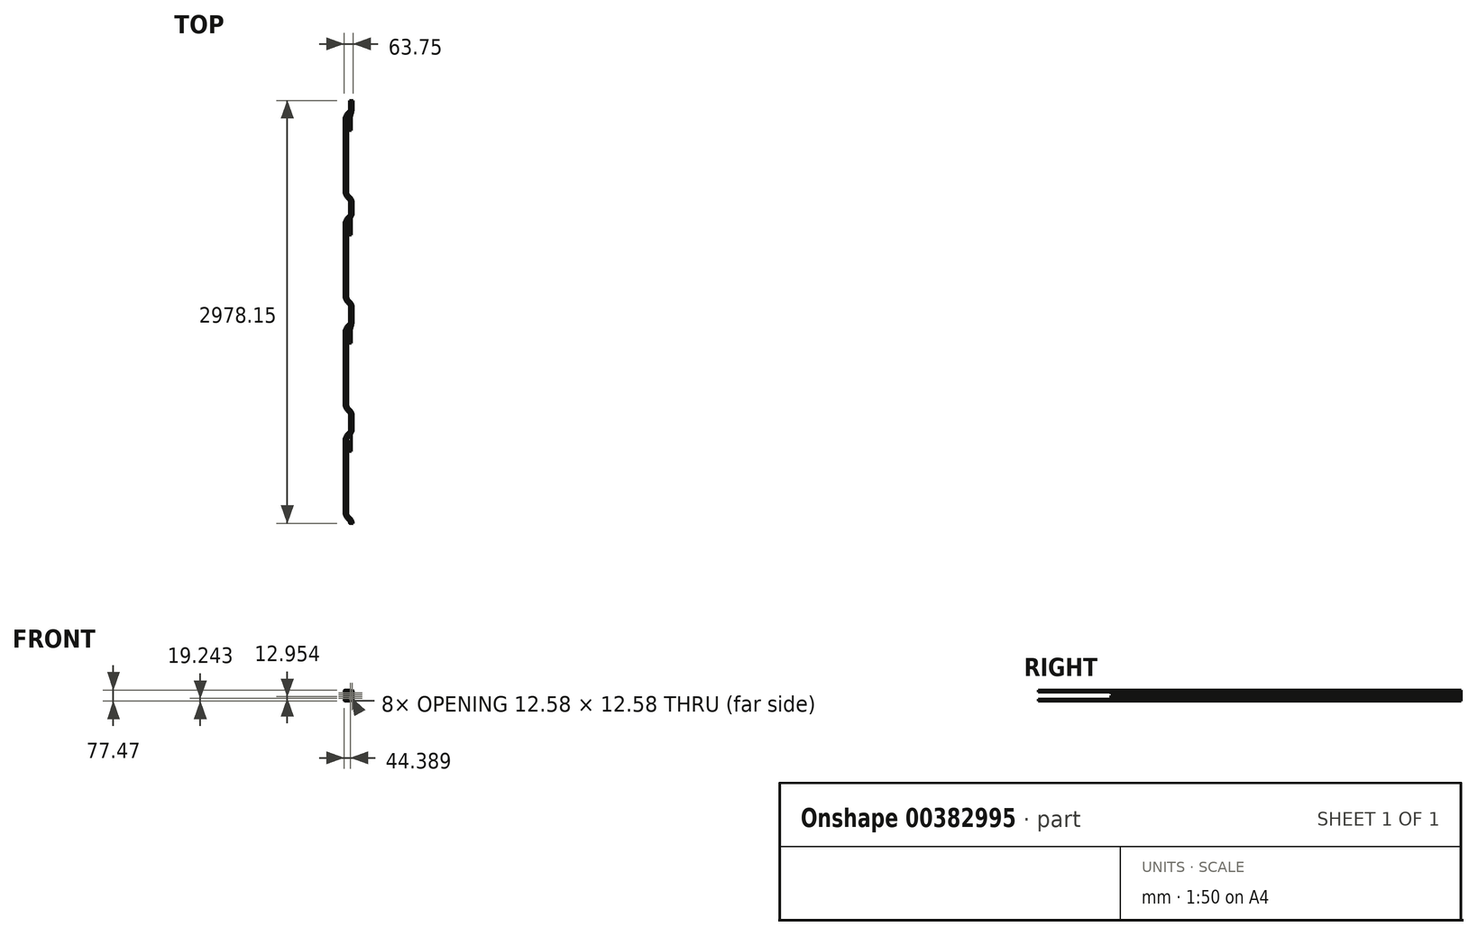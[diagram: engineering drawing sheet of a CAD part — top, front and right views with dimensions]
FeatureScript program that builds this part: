
annotation { "Feature Type Name" : "Feature", "Feature Type Description" : "" }
export const myFeature = defineFeature(function(context is Context, id is Id, definition is map)
    precondition{}
    {
        {
            var Q0;
            Q0=qCreatedBy(makeId("Front.planeOp"),FACE);
            var sketch = newSketch(context, id + "F0", { "sketchPlane" : qUnion([Q0])});
            skCircle(sketch, "E0", {"center": v(0, 0) * mm, "radius": 6.35 * mm});
            skCircle(sketch, "E1.0.1.0", {"center": v(0, -12.95) * mm, "radius": 6.35 * mm});
            skCircle(sketch, "E1.0.2.0", {"center": v(0, -25.9) * mm, "radius": 6.35 * mm});
            skCircle(sketch, "E1.0.3.0", {"center": v(0, -38.86) * mm, "radius": 6.35 * mm});
            skCircle(sketch, "E1.0.4.0", {"center": v(0, -51.82) * mm, "radius": 6.35 * mm});
            skCircle(sketch, "E1.0.5.0", {"center": v(0, -64.77) * mm, "radius": 6.35 * mm});
            skCircle(sketch, "E1.1.0.0", {"center": v(12.95, 0) * mm, "radius": 6.35 * mm});
            skCircle(sketch, "E1.1.1.0", {"center": v(12.95, -12.95) * mm, "radius": 6.35 * mm});
            skCircle(sketch, "E1.1.2.0", {"center": v(12.95, -25.9) * mm, "radius": 6.35 * mm});
            skCircle(sketch, "E1.1.3.0", {"center": v(12.95, -38.86) * mm, "radius": 6.35 * mm});
            skCircle(sketch, "E1.1.4.0", {"center": v(12.95, -51.82) * mm, "radius": 6.35 * mm});
            skCircle(sketch, "E1.1.5.0", {"center": v(12.95, -64.77) * mm, "radius": 6.35 * mm});
            skLineSegment(sketch, "E1.direction1", {"start": v(0, 0) * mm, "end": v(12.95, 0) * mm, "construction": true});
            skLineSegment(sketch, "E1.direction2", {"start": v(0, 0) * mm, "end": v(0, -12.95) * mm, "construction": true});
            skLineSegment(sketch, "E2", {"start": v(12.95, 6.35) * mm, "end": v(0, 6.35) * mm});
            skLineSegment(sketch, "E3", {"start": v(12.95, -71.12) * mm, "end": v(0, -71.12) * mm});
            skLineSegment(sketch, "E4", {"start": v(19.3, -64.77) * mm, "end": v(19.3, 0) * mm});
            skLineSegment(sketch, "E5", {"start": v(-6.35, -64.77) * mm, "end": v(-6.35, 0) * mm});
            skArc(sketch, "E6", {"start": v(-6.35, 0) * mm, "mid": v(-4.5, 4.5) * mm, "end": v(0, 6.35) * mm});
            skArc(sketch, "E7", {"start": v(19.3, 0) * mm, "mid": v(17.44, 4.5) * mm, "end": v(12.95, 6.35) * mm});
            skArc(sketch, "E8", {"start": v(0, -71.12) * mm, "mid": v(-4.5, -69.26) * mm, "end": v(-6.35, -64.77) * mm});
            skArc(sketch, "E9", {"start": v(12.95, -71.12) * mm, "mid": v(17.44, -69.26) * mm, "end": v(19.3, -64.77) * mm});
            skSolve(sketch);
        }
        {
            var Q0;
            {var subQ0=sQuery(id+"F0.wireOp",EDGE,"E1.1.0.0");var subQ1=makeQuery(id+"F0.imprint","INTERSECT",VERTEX,{"derivedFrom":[subQ0,sQuery(id+"F0.wireOp",EDGE,"E2")]});Q0=makeQuery(id+"F0.imprint","IMPRINT",FACE,{"disambiguationData":[TD([[makeQuery(id+"F0.imprint","IMPRINT",EDGE,{"disambiguationData":[TD([[subQ1,1.0]])],"derivedFrom":subQ0}),1.0]])]});}
            var Q1;
            {var subQ0=sQuery(id+"F0.wireOp",EDGE,"E0");var subQ1=makeQuery(id+"F0.imprint","INTERSECT",VERTEX,{"derivedFrom":[subQ0,sQuery(id+"F0.wireOp",EDGE,"E2")]});Q1=makeQuery(id+"F0.imprint","IMPRINT",FACE,{"disambiguationData":[TD([[makeQuery(id+"F0.imprint","IMPRINT",EDGE,{"disambiguationData":[TD([[subQ1,-1.0]])],"derivedFrom":subQ0}),1.0]])]});}
            var Q2;
            Q2=makeQuery(id+"F0.imprint","IMPRINT",FACE,{"disambiguationData":[TD([[makeQuery(id+"F0.imprint","IMPRINT",EDGE,{"derivedFrom":sQuery(id+"F0.wireOp",EDGE,"E1.1.1.0")}),1.0]])]});
            var Q3;
            Q3=makeQuery(id+"F0.imprint","IMPRINT",FACE,{"disambiguationData":[TD([[makeQuery(id+"F0.imprint","IMPRINT",EDGE,{"derivedFrom":sQuery(id+"F0.wireOp",EDGE,"E1.0.1.0")}),1.0]])]});
            var Q4;
            Q4=makeQuery(id+"F0.imprint","IMPRINT",FACE,{"disambiguationData":[TD([[makeQuery(id+"F0.imprint","IMPRINT",EDGE,{"derivedFrom":sQuery(id+"F0.wireOp",EDGE,"E1.1.2.0")}),1.0]])]});
            var Q5;
            Q5=makeQuery(id+"F0.imprint","IMPRINT",FACE,{"disambiguationData":[TD([[makeQuery(id+"F0.imprint","IMPRINT",EDGE,{"derivedFrom":sQuery(id+"F0.wireOp",EDGE,"E1.0.2.0")}),1.0]])]});
            var Q6;
            Q6=makeQuery(id+"F0.imprint","IMPRINT",FACE,{"disambiguationData":[TD([[makeQuery(id+"F0.imprint","IMPRINT",EDGE,{"derivedFrom":sQuery(id+"F0.wireOp",EDGE,"E1.1.3.0")}),1.0]])]});
            var Q7;
            Q7=makeQuery(id+"F0.imprint","IMPRINT",FACE,{"disambiguationData":[TD([[makeQuery(id+"F0.imprint","IMPRINT",EDGE,{"derivedFrom":sQuery(id+"F0.wireOp",EDGE,"E1.0.3.0")}),1.0]])]});
            var Q8;
            Q8=makeQuery(id+"F0.imprint","IMPRINT",FACE,{"disambiguationData":[TD([[makeQuery(id+"F0.imprint","IMPRINT",EDGE,{"derivedFrom":sQuery(id+"F0.wireOp",EDGE,"E1.1.4.0")}),1.0]])]});
            var Q9;
            Q9=makeQuery(id+"F0.imprint","IMPRINT",FACE,{"disambiguationData":[TD([[makeQuery(id+"F0.imprint","IMPRINT",EDGE,{"derivedFrom":sQuery(id+"F0.wireOp",EDGE,"E1.0.4.0")}),1.0]])]});
            var Q10;
            {var subQ0=sQuery(id+"F0.wireOp",EDGE,"E1.1.5.0");var subQ1=makeQuery(id+"F0.imprint","INTERSECT",VERTEX,{"derivedFrom":[subQ0,sQuery(id+"F0.wireOp",EDGE,"E3")]});Q10=makeQuery(id+"F0.imprint","IMPRINT",FACE,{"disambiguationData":[TD([[makeQuery(id+"F0.imprint","IMPRINT",EDGE,{"disambiguationData":[TD([[subQ1,1.0]])],"derivedFrom":subQ0}),1.0]])]});}
            var Q11;
            {var subQ0=sQuery(id+"F0.wireOp",EDGE,"E1.0.5.0");var subQ1=makeQuery(id+"F0.imprint","INTERSECT",VERTEX,{"derivedFrom":[subQ0,sQuery(id+"F0.wireOp",EDGE,"E3")]});Q11=makeQuery(id+"F0.imprint","IMPRINT",FACE,{"disambiguationData":[TD([[makeQuery(id+"F0.imprint","IMPRINT",EDGE,{"disambiguationData":[TD([[subQ1,1.0]])],"derivedFrom":subQ0}),1.0]])]});}
            extrude(context, id + "F1", {"entities" : qUnion([Q0, Q1, Q2, Q3, Q4, Q5, Q6, Q7, Q8, Q9, Q10, Q11]), "oppositeDirection" : true, "depth" : 6.35 * mm});
        }
        {
            var Q0;
            {var subQ24=sQuery(id+"F0.wireOp",EDGE,"E1.0.1.0");Q0=makeQuery(id+"F0.imprint","IMPRINT",FACE,{"disambiguationData":[TD([[makeQuery(id+"F0.imprint","IMPRINT",EDGE,{"derivedFrom":subQ24}),-1.0]])]});}
            var Q1;
            Q1=makeQuery(id+"F0.imprint","IMPRINT",FACE,{"disambiguationData":[TD([[makeQuery(id+"F0.imprint","IMPRINT",EDGE,{"derivedFrom":sQuery(id+"F0.wireOp",EDGE,"E1.1.4.0")}),1.0]])]});
            var Q2;
            Q2=makeQuery(id+"F0.imprint","IMPRINT",FACE,{"disambiguationData":[TD([[makeQuery(id+"F0.imprint","IMPRINT",EDGE,{"derivedFrom":sQuery(id+"F0.wireOp",EDGE,"E1.0.4.0")}),1.0]])]});
            var Q3;
            {var subQ0=sQuery(id+"F0.wireOp",EDGE,"E1.1.5.0");var subQ1=makeQuery(id+"F0.imprint","INTERSECT",VERTEX,{"derivedFrom":[subQ0,sQuery(id+"F0.wireOp",EDGE,"E3")]});Q3=makeQuery(id+"F0.imprint","IMPRINT",FACE,{"disambiguationData":[TD([[makeQuery(id+"F0.imprint","IMPRINT",EDGE,{"disambiguationData":[TD([[subQ1,1.0]])],"derivedFrom":subQ0}),1.0]])]});}
            var Q4;
            {var subQ0=sQuery(id+"F0.wireOp",EDGE,"E1.0.5.0");var subQ1=makeQuery(id+"F0.imprint","INTERSECT",VERTEX,{"derivedFrom":[subQ0,sQuery(id+"F0.wireOp",EDGE,"E3")]});Q4=makeQuery(id+"F0.imprint","IMPRINT",FACE,{"disambiguationData":[TD([[makeQuery(id+"F0.imprint","IMPRINT",EDGE,{"disambiguationData":[TD([[subQ1,1.0]])],"derivedFrom":subQ0}),1.0]])]});}
            var Q5;
            Q5=makeQuery(id+"F0.imprint","IMPRINT",FACE,{"disambiguationData":[TD([[makeQuery(id+"F0.imprint","IMPRINT",EDGE,{"derivedFrom":sQuery(id+"F0.wireOp",EDGE,"E1.0.3.0")}),1.0]])]});
            var Q6;
            Q6=makeQuery(id+"F0.imprint","IMPRINT",FACE,{"disambiguationData":[TD([[makeQuery(id+"F0.imprint","IMPRINT",EDGE,{"derivedFrom":sQuery(id+"F0.wireOp",EDGE,"E1.1.3.0")}),1.0]])]});
            var Q7;
            Q7=makeQuery(id+"F0.imprint","IMPRINT",FACE,{"disambiguationData":[TD([[makeQuery(id+"F0.imprint","IMPRINT",EDGE,{"derivedFrom":sQuery(id+"F0.wireOp",EDGE,"E1.1.2.0")}),1.0]])]});
            var Q8;
            Q8=makeQuery(id+"F0.imprint","IMPRINT",FACE,{"disambiguationData":[TD([[makeQuery(id+"F0.imprint","IMPRINT",EDGE,{"derivedFrom":sQuery(id+"F0.wireOp",EDGE,"E1.0.2.0")}),1.0]])]});
            var Q9;
            Q9=makeQuery(id+"F0.imprint","IMPRINT",FACE,{"disambiguationData":[TD([[makeQuery(id+"F0.imprint","IMPRINT",EDGE,{"derivedFrom":sQuery(id+"F0.wireOp",EDGE,"E1.1.1.0")}),1.0]])]});
            var Q10;
            Q10=makeQuery(id+"F0.imprint","IMPRINT",FACE,{"disambiguationData":[TD([[makeQuery(id+"F0.imprint","IMPRINT",EDGE,{"derivedFrom":sQuery(id+"F0.wireOp",EDGE,"E1.0.1.0")}),1.0]])]});
            var Q11;
            {var subQ0=sQuery(id+"F0.wireOp",EDGE,"E0");var subQ1=makeQuery(id+"F0.imprint","INTERSECT",VERTEX,{"derivedFrom":[subQ0,sQuery(id+"F0.wireOp",EDGE,"E2")]});Q11=makeQuery(id+"F0.imprint","IMPRINT",FACE,{"disambiguationData":[TD([[makeQuery(id+"F0.imprint","IMPRINT",EDGE,{"disambiguationData":[TD([[subQ1,-1.0]])],"derivedFrom":subQ0}),1.0]])]});}
            var Q12;
            {var subQ0=sQuery(id+"F0.wireOp",EDGE,"E1.1.0.0");var subQ1=makeQuery(id+"F0.imprint","INTERSECT",VERTEX,{"derivedFrom":[subQ0,sQuery(id+"F0.wireOp",EDGE,"E2")]});Q12=makeQuery(id+"F0.imprint","IMPRINT",FACE,{"disambiguationData":[TD([[makeQuery(id+"F0.imprint","IMPRINT",EDGE,{"disambiguationData":[TD([[subQ1,1.0]])],"derivedFrom":subQ0}),1.0]])]});}
            extrude(context, id + "F2", {"entities" : qUnion([Q0, Q1, Q2, Q3, Q4, Q5, Q6, Q7, Q8, Q9, Q10, Q11, Q12]), "operationType" : NewBodyOperationType.ADD, "oppositeDirection" : true, "depth" : 3.17 * mm});
        }
        {
            var Q0;
            Q0=qCreatedBy(makeId("Top.planeOp"),FACE);
            var sketch = newSketch(context, id + "F3", { "sketchPlane" : qUnion([Q0])});
            skPoint(sketch, "E10.0", {"position": v(12.95, 0) * mm});
            skPoint(sketch, "E11.0", {"position": v(0, 0) * mm});
            skPoint(sketch, "E12.0", {"position": v(6.48, 0) * mm});
            skLineSegment(sketch, "E13", {"start": v(12.95, 0) * mm, "end": v(12.95, -152.4) * mm});
            skPoint(sketch, "E14", {"position": v(-25.15, -76.2) * mm});
            skFitSpline(sketch, "E15", {"points": [v(-25.15, -76.2) * mm, v(12.95, 0) * mm], "startDerivative": vector(0, 114.3) * mm, "endDerivative": vector(0, 114.3) * mm});
            skPoint(sketch, "E16", {"position": v(-6.1, -38.1) * mm});
            skLineSegment(sketch, "E17", {"start": v(-25.15, -76.2) * mm, "end": v(-25.15, -584.2) * mm});
            skPoint(sketch, "E18", {"position": v(12.95, -660.4) * mm});
            skFitSpline(sketch, "E19", {"points": [v(-25.15, -584.2) * mm, v(12.95, -660.4) * mm], "startDerivative": vector(0, -114.3) * mm, "endDerivative": vector(0, -114.3) * mm});
            skPoint(sketch, "E20", {"position": v(-6.1, -622.3) * mm});
            skLineSegment(sketch, "E21", {"start": v(12.95, -660.4) * mm, "end": v(12.95, -889) * mm});
            skFitSpline(sketch, "E22", {"points": [v(12.95, 0) * mm, v(0, -76.2) * mm], "startDerivative": vector(0, -114.3) * mm, "endDerivative": vector(0, -114.3) * mm});
            skLineSegment(sketch, "E23", {"start": v(0, -76.2) * mm, "end": v(0, -152.4) * mm});
            skLineSegment(sketch, "E24", {"start": v(12.95, -660.4) * mm, "end": v(12.95, -736.6) * mm});
            skPoint(sketch, "E25", {"position": v(-25.15, -812.8) * mm});
            skFitSpline(sketch, "E26", {"points": [v(-25.15, -812.8) * mm, v(12.95, -736.6) * mm], "startDerivative": vector(0, 114.3) * mm, "endDerivative": vector(0, 114.3) * mm});
            skPoint(sketch, "E27", {"position": v(-6.1, -774.7) * mm});
            skLineSegment(sketch, "E28", {"start": v(-25.15, -812.8) * mm, "end": v(-25.15, -1320.8) * mm});
            skPoint(sketch, "E29", {"position": v(12.95, -1397) * mm});
            skPoint(sketch, "E30", {"position": v(-6.1, -1358.9) * mm});
            skLineSegment(sketch, "E31", {"start": v(12.95, -1397) * mm, "end": v(12.95, -1498.6) * mm});
            skPoint(sketch, "E32", {"position": v(-6.1, -1536.7) * mm});
            skPoint(sketch, "E33", {"position": v(-25.15, -1574.8) * mm});
            skPoint(sketch, "E34", {"position": v(12.95, -1498.6) * mm});
            skPoint(sketch, "E35", {"position": v(-25.15, -1320.8) * mm});
            skFitSpline(sketch, "E36", {"points": [v(-25.15, -1320.8) * mm, v(12.95, -1397) * mm], "startDerivative": vector(0, -114.3) * mm, "endDerivative": vector(0, -114.3) * mm});
            skFitSpline(sketch, "E37", {"points": [v(12.95, -1498.6) * mm, v(-25.15, -1574.8) * mm], "startDerivative": vector(0, -114.3) * mm, "endDerivative": vector(0, -114.3) * mm});
            skPoint(sketch, "E38", {"position": v(0, -1574.8) * mm});
            skFitSpline(sketch, "E39", {"points": [v(12.95, -1498.6) * mm, v(0, -1574.8) * mm], "startDerivative": vector(0, -114.3) * mm, "endDerivative": vector(0, -114.3) * mm});
            skLineSegment(sketch, "E40", {"start": v(0, -1574.8) * mm, "end": v(0, -1651) * mm});
            skLineSegment(sketch, "E41", {"start": v(-25.15, -1574.8) * mm, "end": v(-25.15, -2082.8) * mm});
            skPoint(sketch, "E42", {"position": v(12.95, -2159) * mm});
            skPoint(sketch, "E43", {"position": v(12.95, -2260.6) * mm});
            skPoint(sketch, "E44", {"position": v(-25.15, -2336.8) * mm});
            skPoint(sketch, "E45", {"position": v(-25.15, -2844.8) * mm});
            skPoint(sketch, "E46", {"position": v(12.95, -2921) * mm});
            skPoint(sketch, "E47", {"position": v(-25.15, -2120.9) * mm});
            skPoint(sketch, "E48", {"position": v(-25.15, -2298.7) * mm});
            skFitSpline(sketch, "E49", {"points": [v(-25.15, -2082.8) * mm, v(12.95, -2159) * mm], "startDerivative": vector(0, -114.3) * mm, "endDerivative": vector(0, -114.3) * mm});
            skFitSpline(sketch, "E50", {"points": [v(12.95, -2260.6) * mm, v(-25.15, -2336.8) * mm], "startDerivative": vector(0, -114.3) * mm, "endDerivative": vector(0, -114.3) * mm});
            skLineSegment(sketch, "E51", {"start": v(12.95, -2159) * mm, "end": v(12.95, -2260.6) * mm});
            skPoint(sketch, "E52", {"position": v(-25.15, -2882.9) * mm});
            skLineSegment(sketch, "E53", {"start": v(12.95, -2260.6) * mm, "end": v(12.95, -2336.8) * mm});
            skLineSegment(sketch, "E54", {"start": v(12.95, -2336.8) * mm, "end": v(12.95, -2413) * mm});
            skFitSpline(sketch, "E55", {"points": [v(-25.15, -2844.8) * mm, v(12.95, -2921) * mm], "startDerivative": vector(0, -114.3) * mm, "endDerivative": vector(0, -114.3) * mm});
            skLineSegment(sketch, "E56", {"start": v(-25.15, -2336.8) * mm, "end": v(-25.15, -2844.8) * mm});
            skSolve(sketch);
        }
        {
            var Q0;
            Q0=makeQuery(id+"F0.imprint","IMPRINT",FACE,{"disambiguationData":[TD([[makeQuery(id+"F0.imprint","IMPRINT",EDGE,{"derivedFrom":sQuery(id+"F0.wireOp",EDGE,"E1.1.1.0")}),1.0]])]});
            var Q1;
            Q1=makeQuery(id+"F0.imprint","IMPRINT",FACE,{"disambiguationData":[TD([[makeQuery(id+"F0.imprint","IMPRINT",EDGE,{"derivedFrom":sQuery(id+"F0.wireOp",EDGE,"E1.1.3.0")}),1.0]])]});
            var Q2;
            Q2=sQuery(id+"F3.wireOp",EDGE,"E22");
            var Q3;
            Q3=sQuery(id+"F3.wireOp",EDGE,"E23");
            sweep(context, id + "F4", {"operationType" : NewBodyOperationType.ADD, "profiles" : qUnion([Q0, Q1]), "path" : qUnion([Q2, Q3])});
        }
        {
            var Q0;
            {var subQ0=sQuery(id+"F0.wireOp",EDGE,"E0");var subQ1=makeQuery(id+"F0.imprint","INTERSECT",VERTEX,{"derivedFrom":[subQ0,sQuery(id+"F0.wireOp",EDGE,"E2")]});Q0=makeQuery(id+"F0.imprint","IMPRINT",FACE,{"disambiguationData":[TD([[makeQuery(id+"F0.imprint","IMPRINT",EDGE,{"disambiguationData":[TD([[subQ1,-1.0]])],"derivedFrom":subQ0}),1.0]])]});}
            var Q1;
            {var subQ0=sQuery(id+"F0.wireOp",EDGE,"E1.1.0.0");var subQ1=makeQuery(id+"F0.imprint","INTERSECT",VERTEX,{"derivedFrom":[subQ0,sQuery(id+"F0.wireOp",EDGE,"E2")]});Q1=makeQuery(id+"F0.imprint","IMPRINT",FACE,{"disambiguationData":[TD([[makeQuery(id+"F0.imprint","IMPRINT",EDGE,{"disambiguationData":[TD([[subQ1,1.0]])],"derivedFrom":subQ0}),1.0]])]});}
            var Q2;
            Q2=makeQuery(id+"F0.imprint","IMPRINT",FACE,{"disambiguationData":[TD([[makeQuery(id+"F0.imprint","IMPRINT",EDGE,{"derivedFrom":sQuery(id+"F0.wireOp",EDGE,"E1.0.1.0")}),1.0]])]});
            var Q3;
            Q3=makeQuery(id+"F0.imprint","IMPRINT",FACE,{"disambiguationData":[TD([[makeQuery(id+"F0.imprint","IMPRINT",EDGE,{"derivedFrom":sQuery(id+"F0.wireOp",EDGE,"E1.1.2.0")}),1.0]])]});
            var Q4;
            Q4=makeQuery(id+"F0.imprint","IMPRINT",FACE,{"disambiguationData":[TD([[makeQuery(id+"F0.imprint","IMPRINT",EDGE,{"derivedFrom":sQuery(id+"F0.wireOp",EDGE,"E1.0.2.0")}),1.0]])]});
            var Q5;
            Q5=makeQuery(id+"F0.imprint","IMPRINT",FACE,{"disambiguationData":[TD([[makeQuery(id+"F0.imprint","IMPRINT",EDGE,{"derivedFrom":sQuery(id+"F0.wireOp",EDGE,"E1.0.3.0")}),1.0]])]});
            var Q6;
            Q6=makeQuery(id+"F0.imprint","IMPRINT",FACE,{"disambiguationData":[TD([[makeQuery(id+"F0.imprint","IMPRINT",EDGE,{"derivedFrom":sQuery(id+"F0.wireOp",EDGE,"E1.0.4.0")}),1.0]])]});
            var Q7;
            {var subQ0=sQuery(id+"F0.wireOp",EDGE,"E1.0.5.0");var subQ1=makeQuery(id+"F0.imprint","INTERSECT",VERTEX,{"derivedFrom":[subQ0,sQuery(id+"F0.wireOp",EDGE,"E3")]});Q7=makeQuery(id+"F0.imprint","IMPRINT",FACE,{"disambiguationData":[TD([[makeQuery(id+"F0.imprint","IMPRINT",EDGE,{"disambiguationData":[TD([[subQ1,1.0]])],"derivedFrom":subQ0}),1.0]])]});}
            var Q8;
            Q8=makeQuery(id+"F0.imprint","IMPRINT",FACE,{"disambiguationData":[TD([[makeQuery(id+"F0.imprint","IMPRINT",EDGE,{"derivedFrom":sQuery(id+"F0.wireOp",EDGE,"E1.1.4.0")}),1.0]])]});
            var Q9;
            {var subQ0=sQuery(id+"F0.wireOp",EDGE,"E1.1.5.0");var subQ1=makeQuery(id+"F0.imprint","INTERSECT",VERTEX,{"derivedFrom":[subQ0,sQuery(id+"F0.wireOp",EDGE,"E3")]});Q9=makeQuery(id+"F0.imprint","IMPRINT",FACE,{"disambiguationData":[TD([[makeQuery(id+"F0.imprint","IMPRINT",EDGE,{"disambiguationData":[TD([[subQ1,1.0]])],"derivedFrom":subQ0}),1.0]])]});}
            var Q10;
            Q10=sQuery(id+"F3.wireOp",EDGE,"E15");
            var Q11;
            Q11=sQuery(id+"F3.wireOp",EDGE,"E17");
            var Q12;
            Q12=sQuery(id+"F3.wireOp",EDGE,"E19");
            sweep(context, id + "F5", {"operationType" : NewBodyOperationType.ADD, "profiles" : qUnion([Q0, Q1, Q2, Q3, Q4, Q5, Q6, Q7, Q8, Q9]), "path" : qUnion([Q10, Q11, Q12])});
        }
        {
            var Q0;
            Q0=makeQuery(id+"F5.opSweep","CAP_FACE",FACE,{"disambiguationData":[OSD([sQuery(id+"F0.wireOp",EDGE,"E1.0.1.0"),sQuery(id+"F3.wireOp",VERTEX,"E19.end")])],"isStart":false});
            var Q1;
            Q1=makeQuery(id+"F5.opSweep","CAP_FACE",FACE,{"disambiguationData":[OSD([sQuery(id+"F0.wireOp",EDGE,"E1.0.3.0"),sQuery(id+"F3.wireOp",VERTEX,"E19.end")])],"isStart":false});
            var Q2;
            Q2=sQuery(id+"F3.wireOp",EDGE,"E21");
            sweep(context, id + "F6", {"operationType" : NewBodyOperationType.ADD, "profiles" : qUnion([Q0, Q1]), "path" : qUnion([Q2])});
        }
        {
            var Q0;
            Q0=makeQuery(id+"F5.opSweep","CAP_FACE",FACE,{"disambiguationData":[OSD([sQuery(id+"F0.wireOp",EDGE,"E1.1.0.0"),sQuery(id+"F3.wireOp",VERTEX,"E19.end")])],"isStart":false});
            var Q1;
            Q1=makeQuery(id+"F5.opSweep","CAP_FACE",FACE,{"disambiguationData":[OSD([sQuery(id+"F0.wireOp",EDGE,"E0"),sQuery(id+"F3.wireOp",VERTEX,"E19.end")])],"isStart":false});
            var Q2;
            Q2=makeQuery(id+"F5.opSweep","CAP_FACE",FACE,{"disambiguationData":[OSD([sQuery(id+"F0.wireOp",EDGE,"E1.0.2.0"),sQuery(id+"F3.wireOp",VERTEX,"E19.end")])],"isStart":false});
            var Q3;
            Q3=makeQuery(id+"F5.opSweep","CAP_FACE",FACE,{"disambiguationData":[OSD([sQuery(id+"F0.wireOp",EDGE,"E1.1.2.0"),sQuery(id+"F3.wireOp",VERTEX,"E19.end")])],"isStart":false});
            var Q4;
            Q4=makeQuery(id+"F5.opSweep","CAP_FACE",FACE,{"disambiguationData":[OSD([sQuery(id+"F0.wireOp",EDGE,"E1.0.4.0"),sQuery(id+"F3.wireOp",VERTEX,"E19.end")])],"isStart":false});
            var Q5;
            Q5=makeQuery(id+"F5.opSweep","CAP_FACE",FACE,{"disambiguationData":[OSD([sQuery(id+"F0.wireOp",EDGE,"E1.1.4.0"),sQuery(id+"F3.wireOp",VERTEX,"E19.end")])],"isStart":false});
            var Q6;
            Q6=makeQuery(id+"F5.opSweep","CAP_FACE",FACE,{"disambiguationData":[OSD([sQuery(id+"F0.wireOp",EDGE,"E1.0.5.0"),sQuery(id+"F3.wireOp",VERTEX,"E19.end")])],"isStart":false});
            var Q7;
            Q7=makeQuery(id+"F5.opSweep","CAP_FACE",FACE,{"disambiguationData":[OSD([sQuery(id+"F0.wireOp",EDGE,"E1.1.5.0"),sQuery(id+"F3.wireOp",VERTEX,"E19.end")])],"isStart":false});
            var Q8;
            Q8=sQuery(id+"F3.wireOp",EDGE,"E24");
            var Q9;
            Q9=sQuery(id+"F3.wireOp",EDGE,"E26");
            var Q10;
            Q10=sQuery(id+"F3.wireOp",EDGE,"E28");
            var Q11;
            Q11=sQuery(id+"F3.wireOp",EDGE,"E36");
            var Q12;
            Q12=sQuery(id+"F3.wireOp",EDGE,"E31");
            sweep(context, id + "F7", {"operationType" : NewBodyOperationType.ADD, "profiles" : qUnion([Q0, Q1, Q2, Q3, Q4, Q5, Q6, Q7]), "path" : qUnion([Q8, Q9, Q10, Q11, Q12])});
        }
        {
            var Q0;
            Q0=qCreatedBy(makeId("Right.planeOp"),FACE);
            var sketch = newSketch(context, id + "F8", { "sketchPlane" : qUnion([Q0])});
            skFitSpline(sketch, "E57.0", {"points": [v(-1498.6, 0) * mm, v(-1536.7, 0) * mm, v(-1536.7, 0) * mm, v(-1574.8, 0) * mm]});
            skLineSegment(sketch, "E58.0", {"start": v(-1574.8, 0) * mm, "end": v(-1651, 0) * mm});
            skPoint(sketch, "E59", {"position": v(-1651, 12.95) * mm});
            skPoint(sketch, "E60", {"position": v(-1612.9, 6.36) * mm});
            skPoint(sketch, "E60.positionSnap0", {"position": v(-1612.9, 0) * mm});
            skFitSpline(sketch, "E61", {"points": [v(-1574.8, 0) * mm, v(-1651, 12.95) * mm], "startDerivative": vector(-114.3, 0) * mm, "endDerivative": vector(-114.3, 0) * mm});
            skLineSegment(sketch, "E62.0", {"start": v(-2336.8, 0) * mm, "end": v(-2413, 0) * mm});
            skLineSegment(sketch, "E63.0", {"start": v(-2260.6, 0) * mm, "end": v(-2336.8, 0) * mm});
            skPoint(sketch, "E64", {"position": v(-2413, 12.95) * mm});
            skFitSpline(sketch, "E65", {"points": [v(-2336.8, 0) * mm, v(-2413, 12.95) * mm], "startDerivative": vector(-114.3, 0) * mm, "endDerivative": vector(-114.3, 0) * mm});
            skSolve(sketch);
        }
        {
            var Q0;
            Q0=makeQuery(id+"F7.opSweep","CAP_FACE",FACE,{"disambiguationData":[OSD([sQuery(id+"F0.wireOp",EDGE,"E1.1.0.0"),sQuery(id+"F3.wireOp",VERTEX,"E19.end"),sQuery(id+"F3.wireOp",VERTEX,"E31.end")])],"isStart":false});
            var Q1;
            Q1=makeQuery(id+"F7.opSweep","CAP_FACE",FACE,{"disambiguationData":[OSD([sQuery(id+"F0.wireOp",EDGE,"E0"),sQuery(id+"F3.wireOp",VERTEX,"E19.end"),sQuery(id+"F3.wireOp",VERTEX,"E31.end")])],"isStart":false});
            var Q2;
            Q2=makeQuery(id+"F7.opSweep","CAP_FACE",FACE,{"disambiguationData":[OSD([sQuery(id+"F0.wireOp",EDGE,"E1.0.5.0"),sQuery(id+"F3.wireOp",VERTEX,"E19.end"),sQuery(id+"F3.wireOp",VERTEX,"E31.end")])],"isStart":false});
            var Q3;
            Q3=makeQuery(id+"F7.opSweep","CAP_FACE",FACE,{"disambiguationData":[OSD([sQuery(id+"F0.wireOp",EDGE,"E1.1.5.0"),sQuery(id+"F3.wireOp",VERTEX,"E19.end"),sQuery(id+"F3.wireOp",VERTEX,"E31.end")])],"isStart":false});
            var Q4;
            Q4=makeQuery(id+"F7.opSweep","CAP_FACE",FACE,{"disambiguationData":[OSD([sQuery(id+"F0.wireOp",EDGE,"E1.0.4.0"),sQuery(id+"F3.wireOp",VERTEX,"E19.end"),sQuery(id+"F3.wireOp",VERTEX,"E31.end")])],"isStart":false});
            var Q5;
            Q5=makeQuery(id+"F7.opSweep","CAP_FACE",FACE,{"disambiguationData":[OSD([sQuery(id+"F0.wireOp",EDGE,"E1.0.2.0"),sQuery(id+"F3.wireOp",VERTEX,"E19.end"),sQuery(id+"F3.wireOp",VERTEX,"E31.end")])],"isStart":false});
            var Q6;
            Q6=sQuery(id+"F3.wireOp",EDGE,"E37");
            var Q7;
            Q7=sQuery(id+"F3.wireOp",EDGE,"E41");
            var Q8;
            Q8=sQuery(id+"F3.wireOp",EDGE,"E49");
            var Q9;
            Q9=sQuery(id+"F3.wireOp",EDGE,"E51");
            sweep(context, id + "F9", {"operationType" : NewBodyOperationType.ADD, "profiles" : qUnion([Q0, Q1, Q2, Q3, Q4, Q5]), "path" : qUnion([Q6, Q7, Q8, Q9])});
        }
        {
            var Q0;
            Q0=makeQuery(id+"F7.opSweep","CAP_FACE",FACE,{"disambiguationData":[OSD([sQuery(id+"F0.wireOp",EDGE,"E1.1.2.0"),sQuery(id+"F3.wireOp",VERTEX,"E19.end"),sQuery(id+"F3.wireOp",VERTEX,"E31.end")])],"isStart":false});
            var Q1;
            Q1=makeQuery(id+"F7.opSweep","CAP_FACE",FACE,{"disambiguationData":[OSD([sQuery(id+"F0.wireOp",EDGE,"E1.1.4.0"),sQuery(id+"F3.wireOp",VERTEX,"E19.end"),sQuery(id+"F3.wireOp",VERTEX,"E31.end")])],"isStart":false});
            var Q2;
            Q2=sQuery(id+"F3.wireOp",EDGE,"E39");
            var Q3;
            Q3=sQuery(id+"F8.wireOp",EDGE,"E61");
            sweep(context, id + "F10", {"operationType" : NewBodyOperationType.ADD, "profiles" : qUnion([Q0, Q1]), "path" : qUnion([Q2, Q3])});
        }
        {
            var Q0;
            Q0=makeQuery(id+"F9.opSweep","CAP_FACE",FACE,{"disambiguationData":[OSD([sQuery(id+"F0.wireOp",EDGE,"E1.1.0.0"),sQuery(id+"F3.wireOp",VERTEX,"E19.end"),sQuery(id+"F3.wireOp",VERTEX,"E31.end"),sQuery(id+"F3.wireOp",VERTEX,"E51.end")])],"isStart":false});
            var Q1;
            Q1=makeQuery(id+"F9.opSweep","CAP_FACE",FACE,{"disambiguationData":[OSD([sQuery(id+"F0.wireOp",EDGE,"E0"),sQuery(id+"F3.wireOp",VERTEX,"E19.end"),sQuery(id+"F3.wireOp",VERTEX,"E31.end"),sQuery(id+"F3.wireOp",VERTEX,"E51.end")])],"isStart":false});
            var Q2;
            Q2=makeQuery(id+"F9.opSweep","CAP_FACE",FACE,{"disambiguationData":[OSD([sQuery(id+"F0.wireOp",EDGE,"E1.1.5.0"),sQuery(id+"F3.wireOp",VERTEX,"E19.end"),sQuery(id+"F3.wireOp",VERTEX,"E31.end"),sQuery(id+"F3.wireOp",VERTEX,"E51.end")])],"isStart":false});
            var Q3;
            Q3=makeQuery(id+"F9.opSweep","CAP_FACE",FACE,{"disambiguationData":[OSD([sQuery(id+"F0.wireOp",EDGE,"E1.0.5.0"),sQuery(id+"F3.wireOp",VERTEX,"E19.end"),sQuery(id+"F3.wireOp",VERTEX,"E31.end"),sQuery(id+"F3.wireOp",VERTEX,"E51.end")])],"isStart":false});
            var Q4;
            Q4=sQuery(id+"F3.wireOp",EDGE,"E50");
            var Q5;
            Q5=sQuery(id+"F3.wireOp",EDGE,"E56");
            var Q6;
            Q6=sQuery(id+"F3.wireOp",EDGE,"E55");
            sweep(context, id + "F11", {"operationType" : NewBodyOperationType.ADD, "profiles" : qUnion([Q0, Q1, Q2, Q3]), "path" : qUnion([Q4, Q5, Q6])});
        }
        {
            var Q0;
            Q0=makeQuery(id+"F9.opSweep","CAP_FACE",FACE,{"disambiguationData":[OSD([sQuery(id+"F0.wireOp",EDGE,"E1.0.2.0"),sQuery(id+"F3.wireOp",VERTEX,"E19.end"),sQuery(id+"F3.wireOp",VERTEX,"E31.end"),sQuery(id+"F3.wireOp",VERTEX,"E51.end")])],"isStart":false});
            var Q1;
            Q1=makeQuery(id+"F9.opSweep","CAP_FACE",FACE,{"disambiguationData":[OSD([sQuery(id+"F0.wireOp",EDGE,"E1.0.4.0"),sQuery(id+"F3.wireOp",VERTEX,"E19.end"),sQuery(id+"F3.wireOp",VERTEX,"E31.end"),sQuery(id+"F3.wireOp",VERTEX,"E51.end")])],"isStart":false});
            var Q2;
            Q2=sQuery(id+"F8.wireOp",EDGE,"E63.0");
            var Q3;
            Q3=sQuery(id+"F8.wireOp",EDGE,"E65");
            sweep(context, id + "F12", {"operationType" : NewBodyOperationType.ADD, "profiles" : qUnion([Q0, Q1]), "path" : qUnion([Q2, Q3])});
        }
        {
            var Q0;
            Q0=makeQuery(id+"F1.opExtrude","CAP_FACE",FACE,{"disambiguationData":[OSD([sQuery(id+"F0.wireOp",EDGE,"E1.1.0.0")])],"isStart":false});
            var Q1;
            Q1=makeQuery(id+"F1.opExtrude","CAP_FACE",FACE,{"disambiguationData":[OSD([sQuery(id+"F0.wireOp",EDGE,"E0")])],"isStart":false});
            var Q2;
            Q2=makeQuery(id+"F1.opExtrude","CAP_FACE",FACE,{"disambiguationData":[OSD([sQuery(id+"F0.wireOp",EDGE,"E1.1.1.0")])],"isStart":false});
            var Q3;
            Q3=makeQuery(id+"F1.opExtrude","CAP_FACE",FACE,{"disambiguationData":[OSD([sQuery(id+"F0.wireOp",EDGE,"E1.0.1.0")])],"isStart":false});
            var Q4;
            Q4=makeQuery(id+"F1.opExtrude","CAP_FACE",FACE,{"disambiguationData":[OSD([sQuery(id+"F0.wireOp",EDGE,"E1.0.2.0")])],"isStart":false});
            var Q5;
            Q5=makeQuery(id+"F1.opExtrude","CAP_FACE",FACE,{"disambiguationData":[OSD([sQuery(id+"F0.wireOp",EDGE,"E1.1.2.0")])],"isStart":false});
            var Q6;
            Q6=makeQuery(id+"F1.opExtrude","CAP_FACE",FACE,{"disambiguationData":[OSD([sQuery(id+"F0.wireOp",EDGE,"E1.1.3.0")])],"isStart":false});
            var Q7;
            Q7=makeQuery(id+"F1.opExtrude","CAP_FACE",FACE,{"disambiguationData":[OSD([sQuery(id+"F0.wireOp",EDGE,"E1.0.3.0")])],"isStart":false});
            var Q8;
            Q8=makeQuery(id+"F1.opExtrude","CAP_FACE",FACE,{"disambiguationData":[OSD([sQuery(id+"F0.wireOp",EDGE,"E1.1.4.0")])],"isStart":false});
            var Q9;
            Q9=makeQuery(id+"F1.opExtrude","CAP_FACE",FACE,{"disambiguationData":[OSD([sQuery(id+"F0.wireOp",EDGE,"E1.0.4.0")])],"isStart":false});
            var Q10;
            Q10=makeQuery(id+"F1.opExtrude","CAP_FACE",FACE,{"disambiguationData":[OSD([sQuery(id+"F0.wireOp",EDGE,"E1.0.5.0")])],"isStart":false});
            var Q11;
            Q11=makeQuery(id+"F1.opExtrude","CAP_FACE",FACE,{"disambiguationData":[OSD([sQuery(id+"F0.wireOp",EDGE,"E1.1.5.0")])],"isStart":false});
            extrude(context, id + "F13", {"entities" : qUnion([Q0, Q1, Q2, Q3, Q4, Q5, Q6, Q7, Q8, Q9, Q10, Q11]), "operationType" : NewBodyOperationType.ADD, "depth" : 50.8 * mm});
        }
    });
